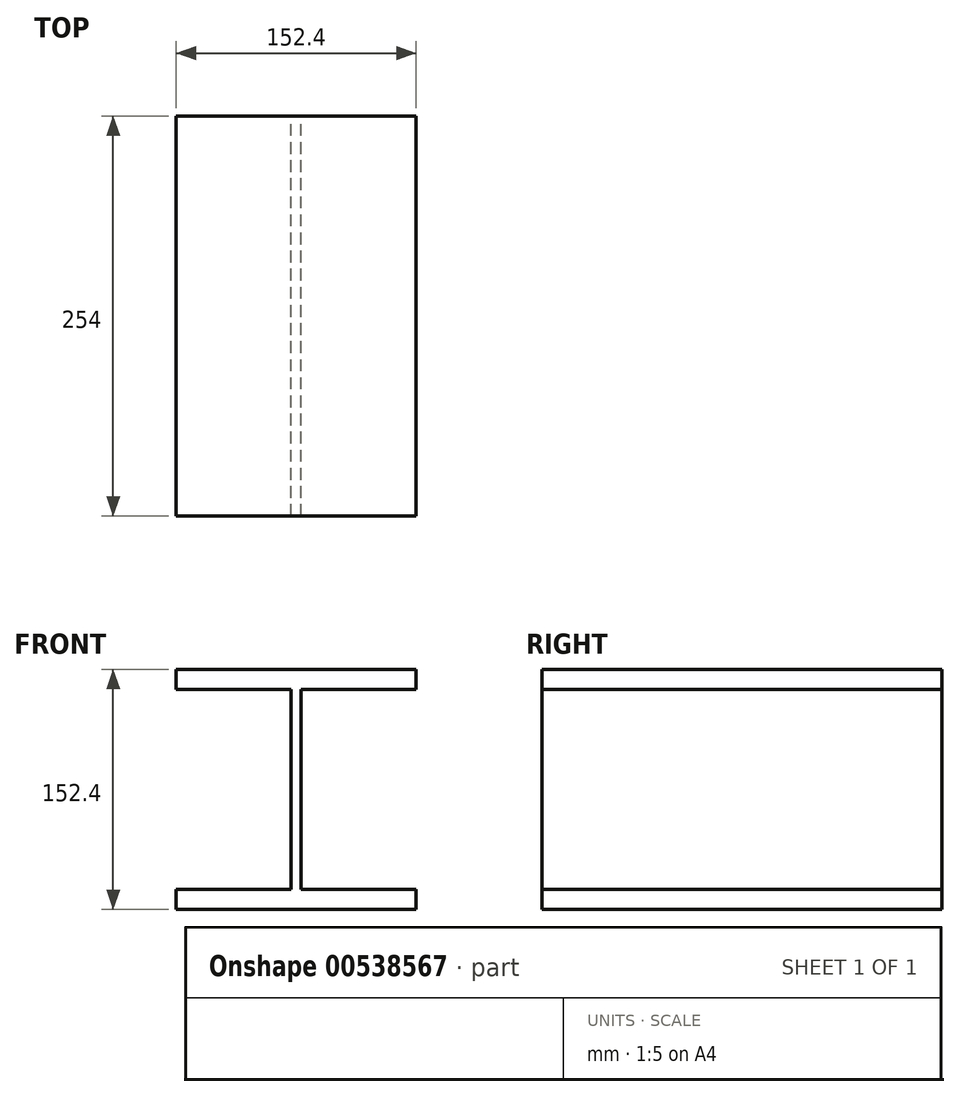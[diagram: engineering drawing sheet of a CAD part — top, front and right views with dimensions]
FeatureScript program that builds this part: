
annotation { "Feature Type Name" : "Feature", "Feature Type Description" : "" }
export const myFeature = defineFeature(function(context is Context, id is Id, definition is map)
    precondition{}
    {
        {
            var Q0;
            Q0=qCreatedBy(makeId("Front.planeOp"),FACE);
            var sketch = newSketch(context, id + "F0", { "sketchPlane" : qUnion([Q0])});
            skLineSegment(sketch, "E0.bottom", {"start": v(3.18, -63.5) * mm, "end": v(-3.17, -63.5) * mm});
            skLineSegment(sketch, "E0.top", {"start": v(3.18, 63.5) * mm, "end": v(-3.17, 63.5) * mm});
            skLineSegment(sketch, "E0.left", {"start": v(3.18, -63.5) * mm, "end": v(3.18, 63.5) * mm});
            skLineSegment(sketch, "E0.right", {"start": v(-3.17, -63.5) * mm, "end": v(-3.17, 63.5) * mm});
            skPoint(sketch, "E0.middle", {"position": v(0, 0) * mm});
            skLineSegment(sketch, "E1.bottom", {"start": v(76.2, 63.5) * mm, "end": v(-76.2, 63.5) * mm});
            skLineSegment(sketch, "E1.top", {"start": v(76.2, 76.2) * mm, "end": v(-76.2, 76.2) * mm});
            skLineSegment(sketch, "E1.left", {"start": v(76.2, 63.5) * mm, "end": v(76.2, 76.2) * mm});
            skLineSegment(sketch, "E1.right", {"start": v(-76.2, 63.5) * mm, "end": v(-76.2, 76.2) * mm});
            skPoint(sketch, "E1.middle", {"position": v(0, 69.85) * mm});
            skLineSegment(sketch, "E2.bottom", {"start": v(76.2, -76.2) * mm, "end": v(-76.2, -76.2) * mm});
            skLineSegment(sketch, "E2.top", {"start": v(76.2, -63.5) * mm, "end": v(-76.2, -63.5) * mm});
            skLineSegment(sketch, "E2.left", {"start": v(76.2, -76.2) * mm, "end": v(76.2, -63.5) * mm});
            skLineSegment(sketch, "E2.right", {"start": v(-76.2, -76.2) * mm, "end": v(-76.2, -63.5) * mm});
            skPoint(sketch, "E2.middle", {"position": v(0, -69.85) * mm});
            skSolve(sketch);
        }
        {
            var Q0;
            Q0=makeQuery(id+"F0.imprint","IMPRINT",FACE,{"disambiguationData":[TD([[makeQuery(id+"F0.imprint","IMPRINT",EDGE,{"derivedFrom":sQuery(id+"F0.wireOp",EDGE,"E2.bottom")}),-1.0]])]});
            var Q1;
            Q1=makeQuery(id+"F0.imprint","IMPRINT",FACE,{"disambiguationData":[TD([[makeQuery(id+"F0.imprint","IMPRINT",EDGE,{"derivedFrom":sQuery(id+"F0.wireOp",EDGE,"E1.top")}),1.0]])]});
            var Q2;
            {var subQ0=sQuery(id+"F0.wireOp",EDGE,"E0.left");Q2=makeQuery(id+"F0.imprint","IMPRINT",FACE,{"disambiguationData":[TD([[makeQuery(id+"F0.imprint","IMPRINT",EDGE,{"derivedFrom":subQ0}),1.0]])]});}
            extrude(context, id + "F1", {"entities" : qUnion([Q0, Q1, Q2]), "depth" : 254 * mm, "offsetDistance" : 25.4 * mm});
        }
    });
